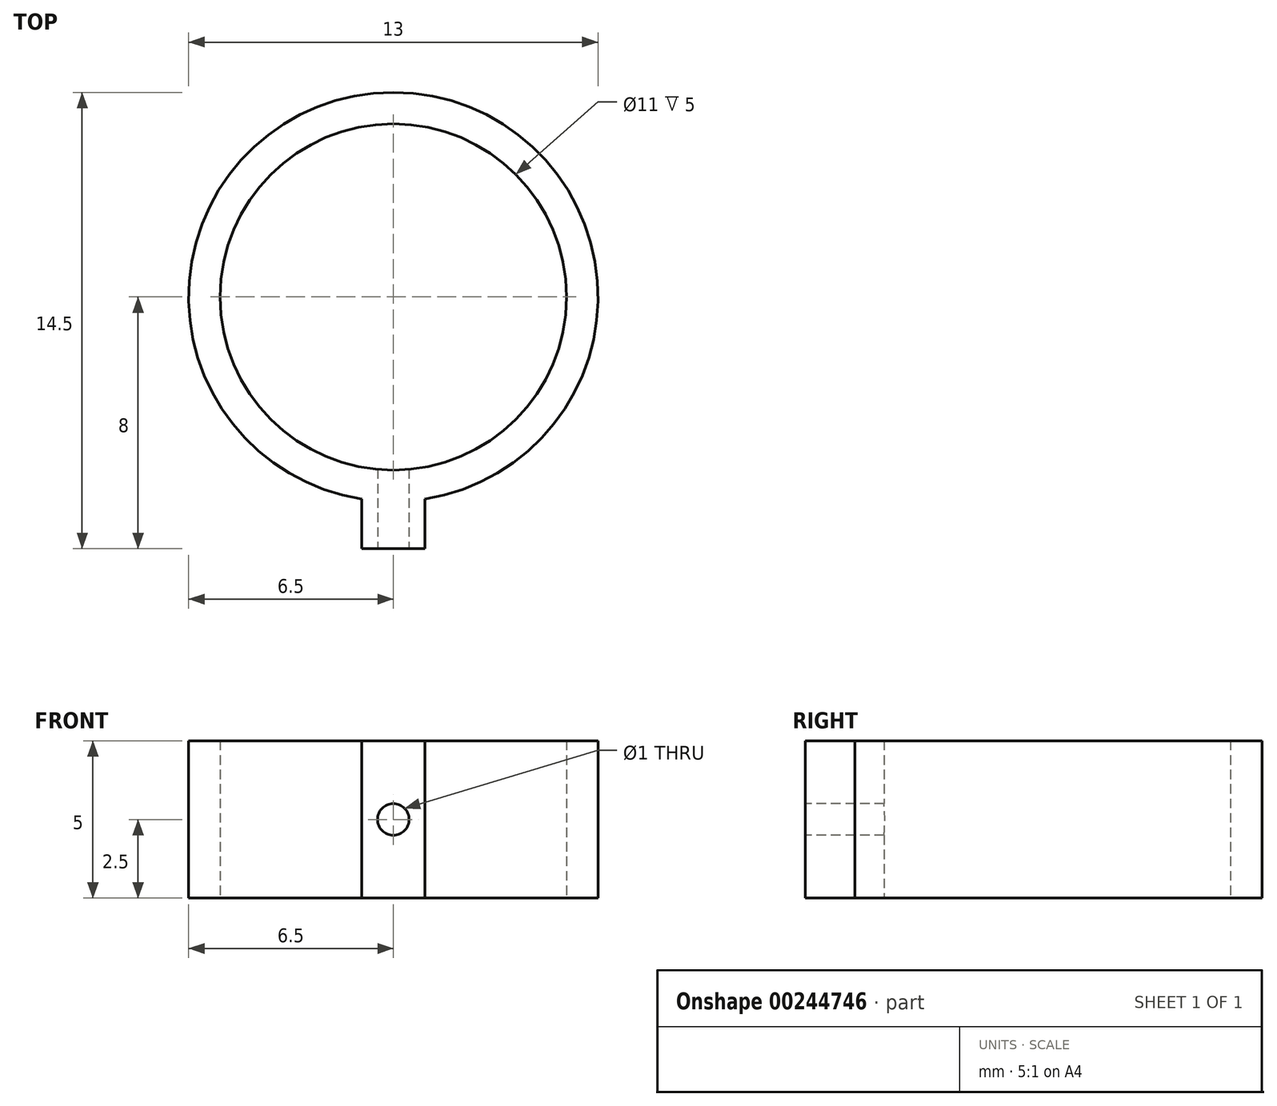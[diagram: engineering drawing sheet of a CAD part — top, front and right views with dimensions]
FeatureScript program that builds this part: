
annotation { "Feature Type Name" : "Feature", "Feature Type Description" : "" }
export const myFeature = defineFeature(function(context is Context, id is Id, definition is map)
    precondition{}
    {
        {
            var Q0;
            Q0=qCreatedBy(makeId("Top.planeOp"),FACE);
            var sketch = newSketch(context, id + "F0", { "sketchPlane" : qUnion([Q0])});
            skArc(sketch, "E0", {"start": v(1, -6.42) * mm, "mid": v(0, 6.5) * mm, "end": v(-1, -6.42) * mm});
            skCircle(sketch, "E1", {"center": v(0, 0) * mm, "radius": 5.5 * mm});
            skLineSegment(sketch, "E2.bottom", {"start": v(1, -8) * mm, "end": v(-1, -8) * mm});
            skLineSegment(sketch, "E2.left", {"start": v(1, -8) * mm, "end": v(1, -6.42) * mm});
            skLineSegment(sketch, "E2.right", {"start": v(-1, -8) * mm, "end": v(-1, -6.42) * mm});
            skSolve(sketch);
        }
        {
            var Q0;
            Q0 = qSketchRegion(id + "F0", true);
            extrude(context, id + "F1", {"entities" : qUnion([Q0]), "depth" : 5 * mm});
        }
        {
            var Q0;
            Q0=makeQuery(id+"F1.opExtrude","SWEPT_FACE",FACE,{"disambiguationData":[OSD([sQuery(id+"F0.wireOp",EDGE,"E2.bottom")])]});
            var sketch = newSketch(context, id + "F2", { "sketchPlane" : qUnion([Q0])});
            skCircle(sketch, "E3", {"center": v(0, 2.5) * mm, "radius": 0.5 * mm});
            skSolve(sketch);
        }
        {
            var Q0;
            Q0 = qSketchRegion(id + "F2", true);
            extrude(context, id + "F3", {"entities" : qUnion([Q0]), "operationType" : NewBodyOperationType.REMOVE, "oppositeDirection" : true, "depth" : 5 * mm});
        }
    });
